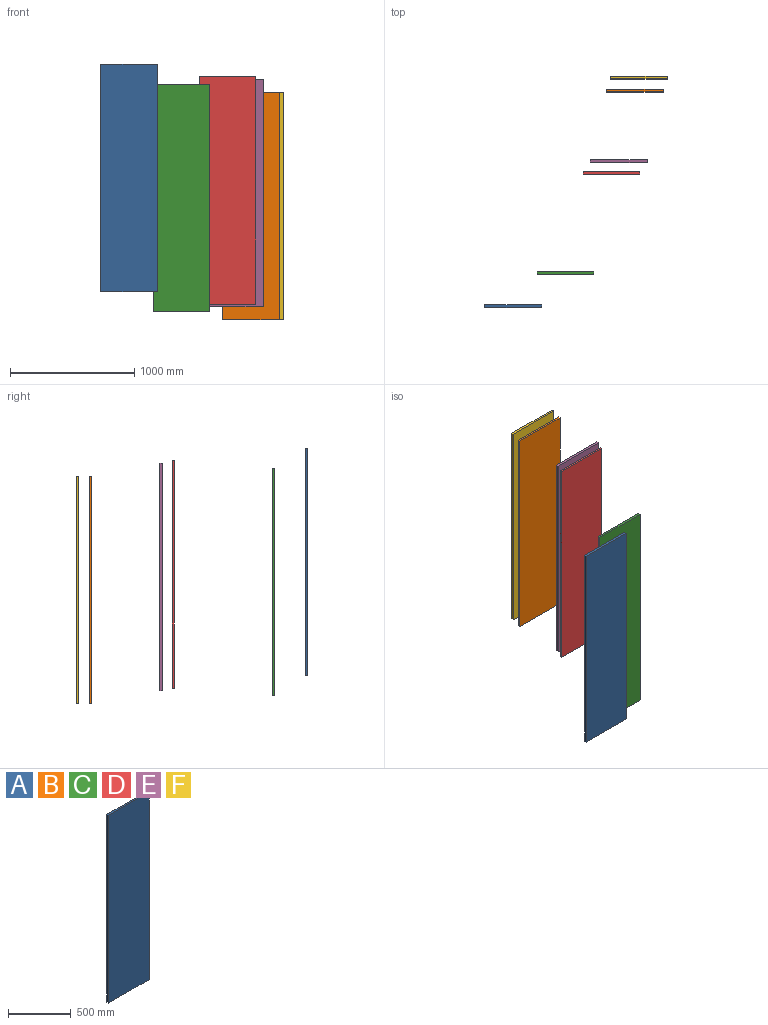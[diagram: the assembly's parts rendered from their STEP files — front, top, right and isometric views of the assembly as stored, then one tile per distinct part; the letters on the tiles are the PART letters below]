
ASSEMBLY  parts=6 mates=1
PART A: 6 faces, bbox 457.2x19.1x1828.8 mm
  f0: plane 457.2x19.05mm, normal (0,0,1), area 8709.7mm2, adj f1,f3,f4,f5
  f1: plane 1828.8x19.05mm, normal (-1,0,0), area 34838.6mm2, adj f0,f2,f4,f5
  f2: plane 457.2x19.05mm, normal (0,0,-1), area 8709.7mm2, adj f1,f3,f4,f5
  f3: plane 1828.8x19.05mm, normal (1,0,0), area 34838.6mm2, adj f0,f2,f4,f5
  f4: plane 1828.8x457.2mm, normal (0,-1,0), area 836127.4mm2, adj f0,f1,f2,f3
  f5: plane 1828.8x457.2mm, normal (0,1,0), area 836127.4mm2, adj f0,f1,f2,f3
PART B: same geometry as A
PART C: same geometry as A
PART D: same geometry as A
PART E: same geometry as A
PART F: same geometry as A
PLACE A t=(-939.75,-784.34,232.65)mm
PLACE B t=(38.91,949.21,10.46)mm
PLACE C t=(-518.36,-518.68,74.41)mm
PLACE D t=(-148.37,285.39,134.47)mm
PLACE E t=(-89.76,382.09,112.46)mm
PLACE F t=(71.45,1052.68,10.46)mm
MATE planar F.f2 <-> B.f2  axis (0,0,-1) through (0.57,1043.16,-956.96)mm
